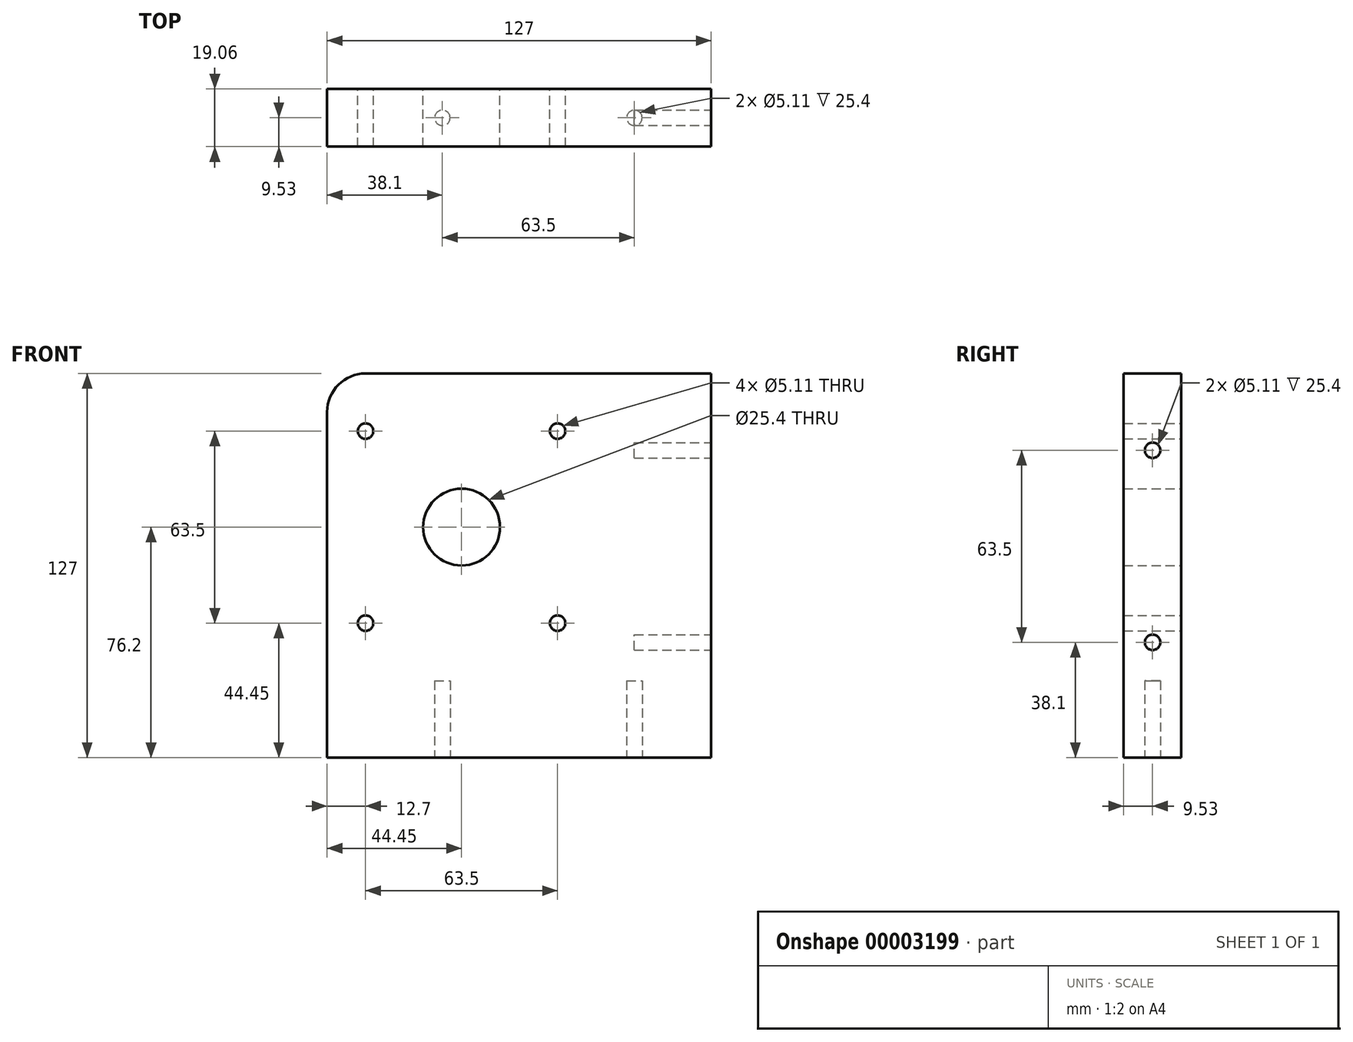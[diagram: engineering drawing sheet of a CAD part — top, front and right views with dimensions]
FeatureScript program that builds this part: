
annotation { "Feature Type Name" : "Feature", "Feature Type Description" : "" }
export const myFeature = defineFeature(function(context is Context, id is Id, definition is map)
    precondition{}
    {
        {
            var Q0;
            Q0=qCreatedBy(makeId("Front.planeOp"),FACE);
            var sketch = newSketch(context, id + "F0", { "sketchPlane" : qUnion([Q0])});
            skLineSegment(sketch, "E0", {"start": v(0, 0) * mm, "end": v(0, -127) * mm});
            skLineSegment(sketch, "E1", {"start": v(0, -127) * mm, "end": v(127, -127) * mm});
            skLineSegment(sketch, "E2", {"start": v(127, -127) * mm, "end": v(127, 0) * mm});
            skLineSegment(sketch, "E3", {"start": v(127, 0) * mm, "end": v(0, 0) * mm});
            skLineSegment(sketch, "E4", {"start": v(12.7, 0) * mm, "end": v(12.7, -127) * mm, "construction": true});
            skLineSegment(sketch, "E5", {"start": v(76.2, 0) * mm, "end": v(76.2, -127) * mm, "construction": true});
            skLineSegment(sketch, "E6", {"start": v(0, -82.55) * mm, "end": v(127, -82.55) * mm, "construction": true});
            skLineSegment(sketch, "E7", {"start": v(0, -19.05) * mm, "end": v(127, -19.05) * mm, "construction": true});
            skCircle(sketch, "E8", {"center": v(12.7, -19.05) * mm, "radius": 2.55 * mm});
            skCircle(sketch, "E9", {"center": v(76.2, -19.05) * mm, "radius": 2.55 * mm});
            skCircle(sketch, "E10", {"center": v(76.2, -82.55) * mm, "radius": 2.55 * mm});
            skCircle(sketch, "E11", {"center": v(12.7, -82.55) * mm, "radius": 2.55 * mm});
            skLineSegment(sketch, "E12", {"start": v(44.45, 0) * mm, "end": v(44.45, -127) * mm, "construction": true});
            skLineSegment(sketch, "E13", {"start": v(127, -50.8) * mm, "end": v(12.7, -50.8) * mm, "construction": true});
            skCircle(sketch, "E14", {"center": v(44.45, -50.8) * mm, "radius": 12.7 * mm});
            skSolve(sketch);
        }
        {
            var Q0;
            Q0 = qSketchRegion(id + "F0", true);
            extrude(context, id + "F1", {"entities" : qUnion([Q0]), "endBound" : BoundingType.SYMMETRIC, "depth" : 19.05 * mm});
        }
        {
            var Q0;
            Q0=makeQuery(id+"F1.opExtrude","SWEPT_FACE",FACE,{"disambiguationData":[OSD([sQuery(id+"F0.wireOp",EDGE,"E1")])]});
            var sketch = newSketch(context, id + "F2", { "sketchPlane" : qUnion([Q0])});
            skLineSegment(sketch, "E15", {"start": v(0, 0) * mm, "end": v(127, 0) * mm, "construction": true});
            skLineSegment(sketch, "E16", {"start": v(38.1, 9.53) * mm, "end": v(38.1, -9.53) * mm, "construction": true});
            skLineSegment(sketch, "E17", {"start": v(101.6, 9.53) * mm, "end": v(101.6, -9.53) * mm, "construction": true});
            skCircle(sketch, "E18", {"center": v(38.1, 0) * mm, "radius": 2.55 * mm});
            skCircle(sketch, "E19", {"center": v(101.6, 0) * mm, "radius": 2.55 * mm});
            skSolve(sketch);
        }
        {
            var Q0;
            Q0 = qSketchRegion(id + "F2", true);
            extrude(context, id + "F3", {"entities" : qUnion([Q0]), "operationType" : NewBodyOperationType.REMOVE, "oppositeDirection" : true, "depth" : 25.4 * mm});
        }
        {
            var Q0;
            Q0=makeQuery(id+"F1.opExtrude","SWEPT_FACE",FACE,{"disambiguationData":[OSD([sQuery(id+"F0.wireOp",EDGE,"E2")])]});
            var sketch = newSketch(context, id + "F4", { "sketchPlane" : qUnion([Q0])});
            skLineSegment(sketch, "E20", {"start": v(0, 0) * mm, "end": v(0, -127) * mm, "construction": true});
            skLineSegment(sketch, "E21", {"start": v(9.53, -25.4) * mm, "end": v(-9.53, -25.4) * mm, "construction": true});
            skLineSegment(sketch, "E22", {"start": v(9.53, -88.9) * mm, "end": v(-9.53, -88.9) * mm, "construction": true});
            skCircle(sketch, "E23", {"center": v(0, -25.4) * mm, "radius": 2.55 * mm});
            skCircle(sketch, "E24", {"center": v(0, -88.9) * mm, "radius": 2.55 * mm});
            skSolve(sketch);
        }
        {
            var Q0;
            Q0 = qSketchRegion(id + "F4", true);
            extrude(context, id + "F5", {"entities" : qUnion([Q0]), "operationType" : NewBodyOperationType.REMOVE, "oppositeDirection" : true, "depth" : 25.4 * mm});
        }
        {
            var Q0;
            Q0=makeQuery(id+"F1.opExtrude","SWEPT_EDGE",EDGE,{"disambiguationData":[OSD([sQuery(id+"F0.wireOp",EDGE,"E0"),sQuery(id+"F0.wireOp",EDGE,"E3")])]});
            fillet(context, id + "F6", {"entities" : qUnion([Q0]), "radius" : 12.7 * mm, "tangentPropagation" : true, "allowEdgeOverflow" : false});
        }
    });
